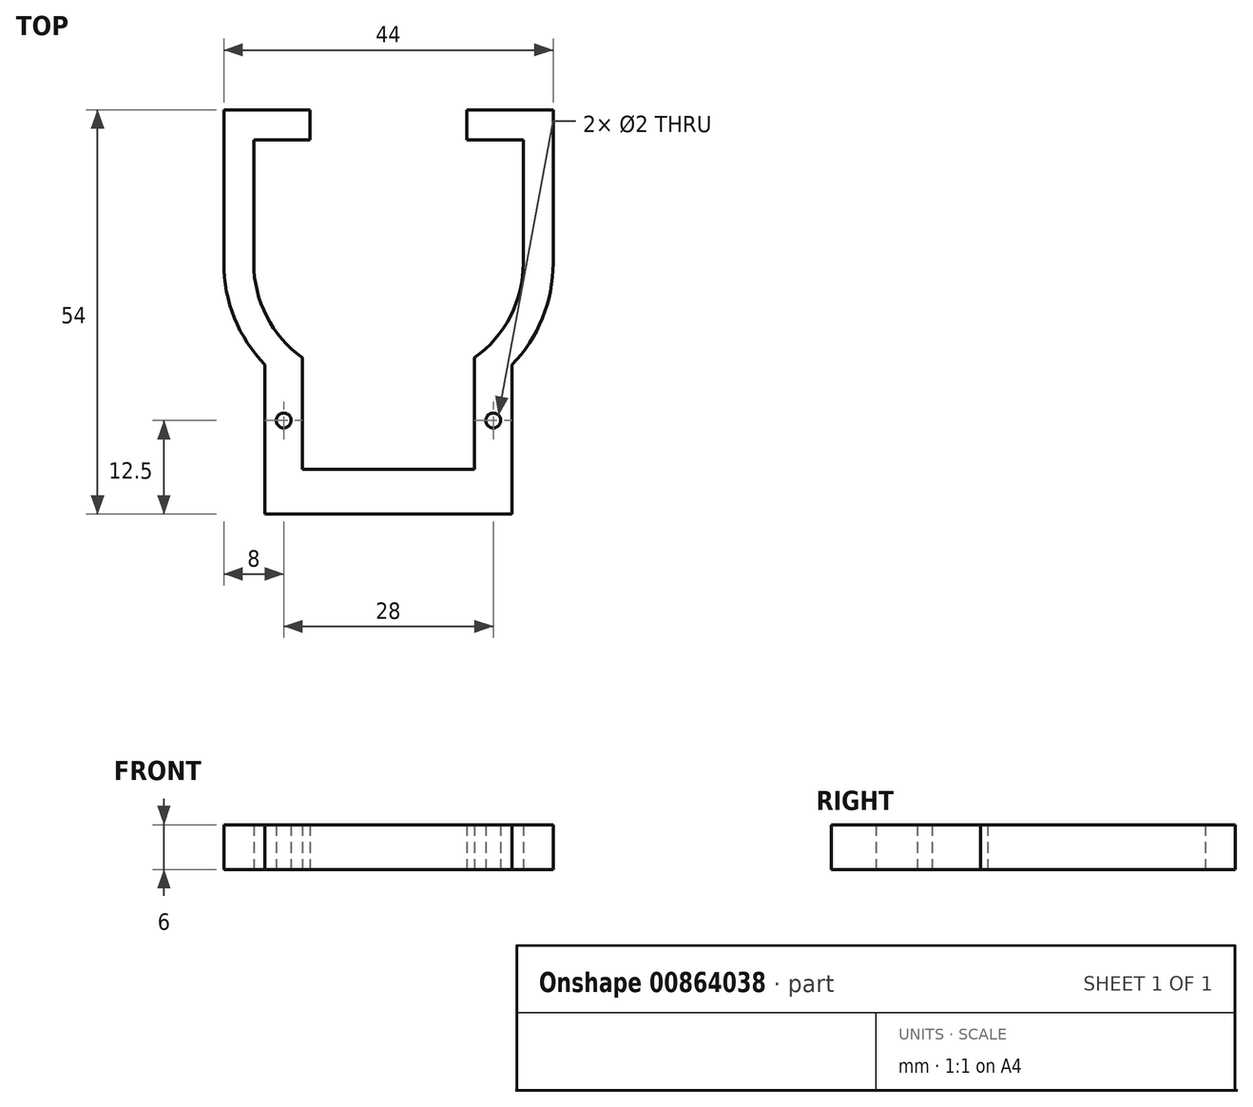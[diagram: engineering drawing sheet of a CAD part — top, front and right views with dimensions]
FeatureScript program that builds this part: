
annotation { "Feature Type Name" : "Feature", "Feature Type Description" : "" }
export const myFeature = defineFeature(function(context is Context, id is Id, definition is map)
    precondition{}
    {
        {
            var Q0;
            Q0=qCreatedBy(makeId("Top.planeOp"),FACE);
            var sketch = newSketch(context, id + "F0", { "sketchPlane" : qUnion([Q0])});
            skLineSegment(sketch, "E0.top", {"start": v(-2.5, -23) * mm, "end": v(2.5, -23) * mm});
            skLineSegment(sketch, "E0.left", {"start": v(-18, 9) * mm, "end": v(-18, -7.5) * mm});
            skLineSegment(sketch, "E0.right", {"start": v(18, 9) * mm, "end": v(18, -7.5) * mm});
            skPoint(sketch, "E1.visualSharp", {"position": v(-18, -23) * mm});
            skArc(sketch, "E1.filletArc", {"start": v(-18, -7.5) * mm, "mid": v(-13.46, -18.46) * mm, "end": v(-2.5, -23) * mm});
            skPoint(sketch, "E2.visualSharp", {"position": v(18, -23) * mm});
            skArc(sketch, "E2.filletArc", {"start": v(2.5, -23) * mm, "mid": v(13.46, -18.46) * mm, "end": v(18, -7.5) * mm});
            skLineSegment(sketch, "E3", {"start": v(-18, 9) * mm, "end": v(18, 9) * mm});
            skLineSegment(sketch, "E4", {"start": v(-18, 9) * mm, "end": v(-8, 9) * mm});
            skLineSegment(sketch, "E5", {"start": v(8, 9) * mm, "end": v(18, 9) * mm});
            skPoint(sketch, "E6", {"position": v(-10.5, 9) * mm});
            skPoint(sketch, "E7", {"position": v(10.5, 9) * mm});
            skLineSegment(sketch, "E8", {"start": v(-18, 9) * mm, "end": v(-10.5, 9) * mm});
            skLineSegment(sketch, "E9", {"start": v(10.5, 9) * mm, "end": v(18, 9) * mm});
            skLineSegment(sketch, "E10.0", {"start": v(-22, 13) * mm, "end": v(-10.5, 13) * mm});
            skLineSegment(sketch, "E10.1", {"start": v(-22, 13) * mm, "end": v(-22, -7.5) * mm});
            skArc(sketch, "E10.2", {"start": v(-22, -7.5) * mm, "mid": v(-16.29, -21.29) * mm, "end": v(-2.5, -27) * mm});
            skLineSegment(sketch, "E10.3", {"start": v(10.5, 13) * mm, "end": v(22, 13) * mm});
            skLineSegment(sketch, "E10.4", {"start": v(22, 13) * mm, "end": v(22, -7.5) * mm});
            skArc(sketch, "E10.5", {"start": v(2.5, -27) * mm, "mid": v(16.29, -21.29) * mm, "end": v(22, -7.5) * mm});
            skLineSegment(sketch, "E10.6", {"start": v(-2.5, -27) * mm, "end": v(2.5, -27) * mm});
            skLineSegment(sketch, "E11", {"start": v(-10.5, 13) * mm, "end": v(-10.5, 9) * mm});
            skLineSegment(sketch, "E12", {"start": v(10.5, 9) * mm, "end": v(10.5, 13) * mm});
            skLineSegment(sketch, "E13.bottom", {"start": v(-11.5, -41) * mm, "end": v(11.5, -41) * mm});
            skLineSegment(sketch, "E13.top", {"start": v(-11.5, -35) * mm, "end": v(11.5, -35) * mm});
            skLineSegment(sketch, "E13.left", {"start": v(11.5, -23) * mm, "end": v(11.5, -29) * mm});
            skLineSegment(sketch, "E13.right", {"start": v(-11.5, -23) * mm, "end": v(-11.5, -29) * mm});
            skLineSegment(sketch, "E14.bottom", {"start": v(11.5, -41) * mm, "end": v(16.5, -41) * mm});
            skLineSegment(sketch, "E14.top", {"start": v(11.5, -23) * mm, "end": v(16.5, -23) * mm});
            skLineSegment(sketch, "E14.left", {"start": v(11.5, -41) * mm, "end": v(11.5, -23) * mm});
            skLineSegment(sketch, "E14.right", {"start": v(16.5, -41) * mm, "end": v(16.5, -23) * mm});
            skLineSegment(sketch, "E15.bottom", {"start": v(-11.5, -41) * mm, "end": v(-16.5, -41) * mm});
            skLineSegment(sketch, "E15.top", {"start": v(-11.5, -23) * mm, "end": v(-16.5, -23) * mm});
            skLineSegment(sketch, "E15.left", {"start": v(-11.5, -41) * mm, "end": v(-11.5, -23) * mm});
            skLineSegment(sketch, "E15.right", {"start": v(-16.5, -41) * mm, "end": v(-16.5, -23) * mm});
            skCircle(sketch, "E16", {"center": v(-14, -28.5) * mm, "radius": 1 * mm});
            skCircle(sketch, "E17", {"center": v(14, -28.5) * mm, "radius": 1 * mm});
            skLineSegment(sketch, "E18", {"start": v(16.5, -23) * mm, "end": v(16.5, -14.15) * mm});
            skLineSegment(sketch, "E19", {"start": v(-16.5, -23) * mm, "end": v(-16.5, -14.15) * mm});
            skLineSegment(sketch, "E20", {"start": v(-11.5, -23) * mm, "end": v(11.5, -23) * mm});
            skLineSegment(sketch, "E21", {"start": v(-11.5, -23) * mm, "end": v(-11.5, -20.12) * mm});
            skLineSegment(sketch, "E22", {"start": v(11.5, -23) * mm, "end": v(11.5, -20.12) * mm});
            skSolve(sketch);
        }
        {
            var Q0;
            {var subQ0=sQuery(id+"F0.wireOp",EDGE,"E0.left");Q0=makeQuery(id+"F0.imprint","IMPRINT",FACE,{"disambiguationData":[TD([[makeQuery(id+"F0.imprint","IMPRINT",EDGE,{"derivedFrom":subQ0}),-1.0]])]});}
            var Q1;
            {var subQ4=sQuery(id+"F0.wireOp",EDGE,"E14.top");Q1=makeQuery(id+"F0.imprint","IMPRINT",FACE,{"disambiguationData":[TD([[makeQuery(id+"F0.imprint","IMPRINT",EDGE,{"derivedFrom":subQ4}),-1.0]])]});}
            var Q2;
            {var subQ0=sQuery(id+"F0.wireOp",EDGE,"E14.bottom");var subQ1=sQuery(id+"F0.wireOp",EDGE,"E10.2");var subQ2=makeQuery(id+"F0.imprint","INTERSECT",VERTEX,{"derivedFrom":[subQ1,subQ0]});Q2=makeQuery(id+"F0.imprint","IMPRINT",FACE,{"disambiguationData":[TD([[makeQuery(id+"F0.imprint","IMPRINT",EDGE,{"disambiguationData":[TD([[subQ2,-1.0]])],"derivedFrom":subQ1}),1.0]])]});}
            var Q3;
            {var subQ1=sQuery(id+"F0.wireOp",EDGE,"E0.right");Q3=makeQuery(id+"F0.imprint","IMPRINT",FACE,{"disambiguationData":[TD([[makeQuery(id+"F0.imprint","IMPRINT",EDGE,{"derivedFrom":subQ1}),1.0]])]});}
            var Q4;
            {var subQ4=sQuery(id+"F0.wireOp",EDGE,"E15.top");Q4=makeQuery(id+"F0.imprint","IMPRINT",FACE,{"disambiguationData":[TD([[makeQuery(id+"F0.imprint","IMPRINT",EDGE,{"derivedFrom":subQ4}),1.0]])]});}
            var Q5;
            {var subQ0=sQuery(id+"F0.wireOp",EDGE,"E15.left");var subQ1=sQuery(id+"F0.wireOp",EDGE,"E10.5");var subQ2=makeQuery(id+"F0.imprint","INTERSECT",VERTEX,{"derivedFrom":[subQ1,subQ0]});Q5=makeQuery(id+"F0.imprint","IMPRINT",FACE,{"disambiguationData":[TD([[makeQuery(id+"F0.imprint","IMPRINT",EDGE,{"disambiguationData":[TD([[subQ2,-1.0]])],"derivedFrom":subQ1}),1.0]])]});}
            var Q6;
            {var subQ1=sQuery(id+"F0.wireOp",EDGE,"E15.bottom");Q6=makeQuery(id+"F0.imprint","IMPRINT",FACE,{"disambiguationData":[TD([[makeQuery(id+"F0.imprint","IMPRINT",EDGE,{"derivedFrom":subQ1}),-1.0]])]});}
            var Q7;
            {var subQ0=sQuery(id+"F0.wireOp",EDGE,"E19");var subQ1=sQuery(id+"F0.wireOp",EDGE,"E10.2");var subQ2=makeQuery(id+"F0.imprint","INTERSECT",VERTEX,{"derivedFrom":[subQ1,subQ0]});Q7=makeQuery(id+"F0.imprint","IMPRINT",FACE,{"disambiguationData":[TD([[makeQuery(id+"F0.imprint","IMPRINT",EDGE,{"disambiguationData":[TD([[subQ2,-1.0]])],"derivedFrom":subQ1}),-1.0]])]});}
            var Q8;
            {var subQ1=sQuery(id+"F0.wireOp",EDGE,"E14.bottom");Q8=makeQuery(id+"F0.imprint","IMPRINT",FACE,{"disambiguationData":[TD([[makeQuery(id+"F0.imprint","IMPRINT",EDGE,{"derivedFrom":subQ1}),1.0]])]});}
            var Q9;
            {var subQ0=sQuery(id+"F0.wireOp",EDGE,"E13.bottom");Q9=makeQuery(id+"F0.imprint","IMPRINT",FACE,{"disambiguationData":[TD([[makeQuery(id+"F0.imprint","IMPRINT",EDGE,{"derivedFrom":subQ0}),1.0]])]});}
            var Q10;
            {var subQ0=sQuery(id+"F0.wireOp",EDGE,"E18");var subQ1=sQuery(id+"F0.wireOp",EDGE,"E10.5");var subQ2=makeQuery(id+"F0.imprint","INTERSECT",VERTEX,{"derivedFrom":[subQ1,subQ0]});Q10=makeQuery(id+"F0.imprint","IMPRINT",FACE,{"disambiguationData":[TD([[makeQuery(id+"F0.imprint","IMPRINT",EDGE,{"disambiguationData":[TD([[subQ2,1.0]])],"derivedFrom":subQ1}),-1.0]])]});}
            var Q11;
            {var subQ7=sQuery(id+"F0.wireOp",EDGE,"E22");Q11=makeQuery(id+"F0.imprint","IMPRINT",FACE,{"disambiguationData":[TD([[makeQuery(id+"F0.imprint","IMPRINT",EDGE,{"derivedFrom":subQ7}),-1.0]])]});}
            var Q12;
            {var subQ0=sQuery(id+"F0.wireOp",EDGE,"E21");Q12=makeQuery(id+"F0.imprint","IMPRINT",FACE,{"disambiguationData":[TD([[makeQuery(id+"F0.imprint","IMPRINT",EDGE,{"derivedFrom":subQ0}),1.0]])]});}
            extrude(context, id + "F1", {"entities" : qUnion([Q0, Q1, Q2, Q3, Q4, Q5, Q6, Q7, Q8, Q9, Q10, Q11, Q12]), "depth" : 6 * mm, "offsetDistance" : 25 * mm});
        }
    });
